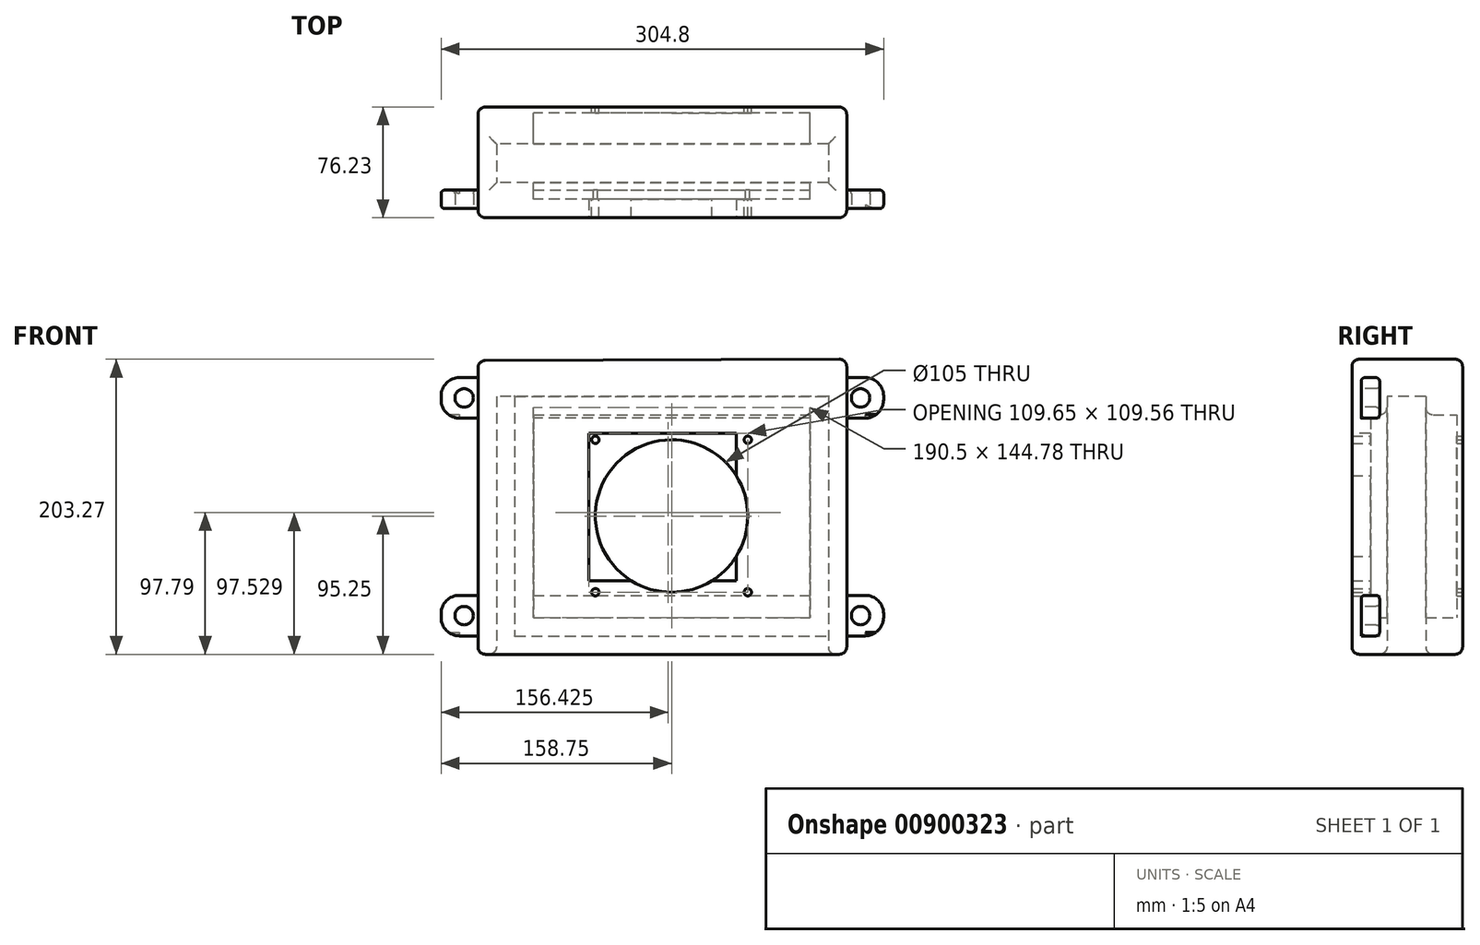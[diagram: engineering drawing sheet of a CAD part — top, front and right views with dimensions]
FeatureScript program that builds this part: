
annotation { "Feature Type Name" : "Feature", "Feature Type Description" : "" }
export const myFeature = defineFeature(function(context is Context, id is Id, definition is map)
    precondition{}
    {
        {
            var Q0;
            Q0=qCreatedBy(makeId("Front.planeOp"),FACE);
            var sketch = newSketch(context, id + "F0", { "sketchPlane" : qUnion([Q0])});
            skLineSegment(sketch, "E0", {"start": v(0, 202.37) * mm, "end": v(0, 0) * mm});
            skLineSegment(sketch, "E1", {"start": v(0, 0) * mm, "end": v(254, 0) * mm});
            skLineSegment(sketch, "E2", {"start": v(254, 0) * mm, "end": v(254, 203.3) * mm});
            skLineSegment(sketch, "E3", {"start": v(254, 203.3) * mm, "end": v(0, 202.37) * mm});
            skLineSegment(sketch, "E4.bottom", {"start": v(228.6, 165.1) * mm, "end": v(38.1, 165.1) * mm});
            skLineSegment(sketch, "E4.top", {"start": v(228.6, 25.4) * mm, "end": v(38.1, 25.4) * mm});
            skLineSegment(sketch, "E4.left", {"start": v(228.6, 165.1) * mm, "end": v(228.6, 25.4) * mm});
            skLineSegment(sketch, "E4.right", {"start": v(38.1, 165.1) * mm, "end": v(38.1, 25.4) * mm});
            skLineSegment(sketch, "E5.bottom", {"start": v(25.4, 177.8) * mm, "end": v(241.3, 177.8) * mm});
            skLineSegment(sketch, "E5.top", {"start": v(25.4, 12.7) * mm, "end": v(241.3, 12.7) * mm});
            skLineSegment(sketch, "E5.left", {"start": v(25.4, 177.8) * mm, "end": v(25.4, 12.7) * mm});
            skLineSegment(sketch, "E5.right", {"start": v(241.3, 177.8) * mm, "end": v(241.3, 12.7) * mm});
            skSolve(sketch);
        }
        {
            var Q0;
            Q0=makeQuery(id+"F0.imprint","IMPRINT",FACE,{"disambiguationData":[TD([[makeQuery(id+"F0.imprint","IMPRINT",EDGE,{"derivedFrom":sQuery(id+"F0.wireOp",EDGE,"E0")}),1.0]])]});
            var Q1;
            Q1=makeQuery(id+"F0.imprint","IMPRINT",FACE,{"disambiguationData":[TD([[makeQuery(id+"F0.imprint","IMPRINT",EDGE,{"derivedFrom":sQuery(id+"F0.wireOp",EDGE,"E4.bottom")}),-1.0]])]});
            extrude(context, id + "F1", {"entities" : qUnion([Q0, Q1]), "depth" : 76.2 * mm, "offsetDistance" : 25.4 * mm});
        }
        {
            var Q0;
            Q0=makeQuery(id+"F1.opExtrude","SWEPT_FACE",FACE,{"disambiguationData":[OSD([sQuery(id+"F0.wireOp",EDGE,"E1")])]});
            var sketch = newSketch(context, id + "F2", { "sketchPlane" : qUnion([Q0])});
            skLineSegment(sketch, "E6.bottom", {"start": v(12.7, 52.07) * mm, "end": v(241.3, 52.07) * mm});
            skLineSegment(sketch, "E6.top", {"start": v(12.7, 25.4) * mm, "end": v(241.3, 25.4) * mm});
            skLineSegment(sketch, "E6.left", {"start": v(12.7, 52.07) * mm, "end": v(12.7, 25.4) * mm});
            skLineSegment(sketch, "E6.right", {"start": v(241.3, 52.07) * mm, "end": v(241.3, 25.4) * mm});
            skSolve(sketch);
        }
        {
            var Q0;
            Q0=makeQuery(id+"F0.imprint","IMPRINT",FACE,{"disambiguationData":[TD([[makeQuery(id+"F0.imprint","IMPRINT",EDGE,{"derivedFrom":sQuery(id+"F0.wireOp",EDGE,"E4.bottom")}),-1.0]])]});
            var Q1;
            Q1=makeQuery(id+"F0.imprint","IMPRINT",FACE,{"disambiguationData":[TD([[makeQuery(id+"F0.imprint","IMPRINT",EDGE,{"derivedFrom":sQuery(id+"F0.wireOp",EDGE,"E4.bottom")}),1.0]])]});
            extrude(context, id + "F3", {"entities" : qUnion([Q0, Q1]), "operationType" : NewBodyOperationType.ADD, "oppositeDirection" : true, "depth" : 0.03 * mm, "offsetDistance" : 25.4 * mm, "hasSecondDirection" : true, "secondDirectionOppositeDirection" : false, "secondDirectionDepth" : 4 * mm});
        }
        {
            var Q0;
            Q0=makeQuery(id+"F3.opExtrude","CAP_FACE",FACE,{"disambiguationData":[OSD([sQuery(id+"F0.wireOp",EDGE,"E5.bottom"),sQuery(id+"F0.wireOp",EDGE,"E5.top"),sQuery(id+"F0.wireOp",EDGE,"E5.left"),sQuery(id+"F0.wireOp",EDGE,"E5.right")])],"isStart":false});
            var sketch = newSketch(context, id + "F4", { "sketchPlane" : qUnion([Q0])});
            skCircle(sketch, "E7", {"center": v(-133.35, 95.25) * mm, "radius": 52.5 * mm});
            skLineSegment(sketch, "E8", {"start": v(-133.35, 95.25) * mm, "end": v(-25.4, 95.25) * mm, "construction": true});
            skLineSegment(sketch, "E9", {"start": v(-133.35, 95.25) * mm, "end": v(-241.3, 95.25) * mm, "construction": true});
            skLineSegment(sketch, "E10", {"start": v(-133.35, 95.25) * mm, "end": v(-133.35, 12.7) * mm, "construction": true});
            skCircle(sketch, "E11", {"center": v(-185.85, 42.75) * mm, "radius": 2.54 * mm});
            skCircle(sketch, "E12", {"center": v(-185.85, 147.75) * mm, "radius": 2.54 * mm});
            skCircle(sketch, "E13", {"center": v(-80.85, 42.75) * mm, "radius": 2.54 * mm});
            skCircle(sketch, "E14", {"center": v(-80.85, 147.75) * mm, "radius": 2.54 * mm});
            skLineSegment(sketch, "E15", {"start": v(-185.85, 42.75) * mm, "end": v(-185.85, 95.25) * mm, "construction": true});
            skLineSegment(sketch, "E16", {"start": v(-185.85, 95.25) * mm, "end": v(-185.85, 147.75) * mm, "construction": true});
            skLineSegment(sketch, "E17", {"start": v(-185.85, 147.75) * mm, "end": v(-133.35, 147.75) * mm, "construction": true});
            skLineSegment(sketch, "E18", {"start": v(-133.35, 147.75) * mm, "end": v(-80.85, 147.75) * mm, "construction": true});
            skLineSegment(sketch, "E19", {"start": v(-80.85, 147.75) * mm, "end": v(-80.85, 177.8) * mm, "construction": true});
            skLineSegment(sketch, "E20", {"start": v(-80.85, 42.75) * mm, "end": v(-80.85, 12.7) * mm, "construction": true});
            skSolve(sketch);
        }
        {
            var Q0;
            Q0=makeQuery(id+"F4.imprint","IMPRINT",FACE,{"disambiguationData":[TD([[makeQuery(id+"F4.imprint","IMPRINT",EDGE,{"derivedFrom":sQuery(id+"F4.wireOp",EDGE,"E7")}),1.0]])]});
            var Q1;
            Q1=makeQuery(id+"F4.imprint","IMPRINT",FACE,{"disambiguationData":[TD([[makeQuery(id+"F4.imprint","IMPRINT",EDGE,{"derivedFrom":sQuery(id+"F4.wireOp",EDGE,"E11")}),1.0]])]});
            var Q2;
            Q2=makeQuery(id+"F4.imprint","IMPRINT",FACE,{"disambiguationData":[TD([[makeQuery(id+"F4.imprint","IMPRINT",EDGE,{"derivedFrom":sQuery(id+"F4.wireOp",EDGE,"E12")}),1.0]])]});
            var Q3;
            Q3=makeQuery(id+"F4.imprint","IMPRINT",FACE,{"disambiguationData":[TD([[makeQuery(id+"F4.imprint","IMPRINT",EDGE,{"derivedFrom":sQuery(id+"F4.wireOp",EDGE,"E13")}),1.0]])]});
            var Q4;
            Q4=makeQuery(id+"F4.imprint","IMPRINT",FACE,{"disambiguationData":[TD([[makeQuery(id+"F4.imprint","IMPRINT",EDGE,{"derivedFrom":sQuery(id+"F4.wireOp",EDGE,"E14")}),1.0]])]});
            extrude(context, id + "F5", {"entities" : qUnion([Q0, Q1, Q2, Q3, Q4]), "operationType" : NewBodyOperationType.REMOVE, "endBound" : BoundingType.THROUGH_ALL, "oppositeDirection" : true, "depth" : 25.4 * mm, "offsetDistance" : 25.4 * mm});
        }
        {
            var Q0;
            Q0=makeQuery(id+"F1.opExtrude","SWEPT_FACE",FACE,{"disambiguationData":[OSD([sQuery(id+"F0.wireOp",EDGE,"E0")])]});
            var sketch = newSketch(context, id + "F6", { "sketchPlane" : qUnion([Q0])});
            skLineSegment(sketch, "E21.bottom", {"start": v(69.85, 12.7) * mm, "end": v(57.15, 12.7) * mm});
            skLineSegment(sketch, "E21.top", {"start": v(69.85, 40.64) * mm, "end": v(57.15, 40.64) * mm});
            skLineSegment(sketch, "E21.left", {"start": v(69.85, 12.7) * mm, "end": v(69.85, 40.64) * mm});
            skLineSegment(sketch, "E21.right", {"start": v(57.15, 12.7) * mm, "end": v(57.15, 40.64) * mm});
            skLineSegment(sketch, "E22.bottom", {"start": v(69.85, 162.65) * mm, "end": v(57.15, 162.65) * mm});
            skLineSegment(sketch, "E22.top", {"start": v(69.85, 190.6) * mm, "end": v(57.15, 190.6) * mm});
            skLineSegment(sketch, "E22.left", {"start": v(69.85, 162.65) * mm, "end": v(69.85, 190.6) * mm});
            skLineSegment(sketch, "E22.right", {"start": v(57.15, 162.65) * mm, "end": v(57.15, 190.6) * mm});
            skSolve(sketch);
        }
        {
            var Q0;
            Q0=makeQuery(id+"F6.imprint","IMPRINT",FACE,{"disambiguationData":[TD([[makeQuery(id+"F6.imprint","IMPRINT",EDGE,{"derivedFrom":sQuery(id+"F6.wireOp",EDGE,"E21.bottom")}),-1.0]])]});
            var Q1;
            Q1=makeQuery(id+"F6.imprint","IMPRINT",FACE,{"disambiguationData":[TD([[makeQuery(id+"F6.imprint","IMPRINT",EDGE,{"derivedFrom":sQuery(id+"F6.wireOp",EDGE,"E22.bottom")}),-1.0]])]});
            var Q2;
            Q2=makeQuery(id+"F1.opExtrude","SWEPT_FACE",FACE,{"disambiguationData":[OSD([sQuery(id+"F0.wireOp",EDGE,"E2")])]});
            var Q3;
            Q3=makeQuery(id+"F1.opExtrude","SWEPT_FACE",FACE,{"disambiguationData":[OSD([sQuery(id+"F0.wireOp",EDGE,"E2")])]});
            extrude(context, id + "F7", {"entities" : qUnion([Q0, Q1]), "operationType" : NewBodyOperationType.ADD, "depth" : 25.4 * mm, "endBoundEntityFace" : qUnion([Q2]), "hasOffset" : true, "offsetDistance" : 25.4 * mm, "hasSecondDirection" : true, "secondDirectionBound" : SecondDirectionBoundingType.UP_TO_SURFACE, "secondDirectionOppositeDirection" : true, "secondDirectionDepth" : 25.4 * mm, "secondDirectionBoundEntityFace" : qUnion([Q3]), "hasSecondDirectionOffset" : true, "secondDirectionOffsetDistance" : 25.4 * mm, "secondDirectionOffsetOppositeDirection" : true});
        }
        {
            var Q0;
            {var subQ2=sQuery(id+"F6.wireOp",EDGE,"E21.left");Q0=makeQuery(id+"F7.boolean.opBoolean","SPLIT",FACE,{"disambiguationData":[TD([makeQuery(id+"F1.opExtrude","SWEPT_FACE",FACE,{"disambiguationData":[OSD([sQuery(id+"F0.wireOp",EDGE,"E2")])]})])],"derivedFrom":makeQuery(id+"F7.opExtrude","SWEPT_FACE",FACE,{"disambiguationData":[OSD([subQ2])]})});}
            var sketch = newSketch(context, id + "F8", { "sketchPlane" : qUnion([Q0])});
            skPoint(sketch, "E23.centerSnap0", {"position": v(279.4, 26.67) * mm});
            skCircle(sketch, "E24", {"center": v(-9.52, 26.67) * mm, "radius": 6.35 * mm});
            skCircle(sketch, "E25", {"center": v(263.53, 176.62) * mm, "radius": 6.35 * mm});
            skCircle(sketch, "E26", {"center": v(-9.52, 176.62) * mm, "radius": 6.35 * mm});
            skLineSegment(sketch, "E27", {"start": v(263.53, 176.62) * mm, "end": v(279.4, 176.62) * mm, "construction": true});
            skLineSegment(sketch, "E28", {"start": v(-9.52, 176.62) * mm, "end": v(-25.4, 176.62) * mm, "construction": true});
            skCircle(sketch, "E29", {"center": v(263.53, 26.67) * mm, "radius": 6.35 * mm});
            skSolve(sketch);
        }
        {
            var Q0;
            Q0=makeQuery(id+"F2.imprint","IMPRINT",FACE,{"disambiguationData":[TD([[makeQuery(id+"F2.imprint","IMPRINT",EDGE,{"derivedFrom":sQuery(id+"F2.wireOp",EDGE,"E6.bottom")}),-1.0]])]});
            var Q1;
            Q1=makeQuery(id+"F1.opExtrude","SWEPT_FACE",FACE,{"disambiguationData":[OSD([sQuery(id+"F0.wireOp",EDGE,"E4.bottom")])]});
            extrude(context, id + "F9", {"entities" : qUnion([Q0]), "operationType" : NewBodyOperationType.REMOVE, "endBound" : BoundingType.UP_TO_SURFACE, "oppositeDirection" : true, "depth" : 209.55 * mm, "endBoundEntityFace" : qUnion([Q1]), "hasOffset" : true, "offsetDistance" : 12.7 * mm, "offsetOppositeDirection" : true});
        }
        {
            var Q0;
            Q0=makeQuery(id+"F2.imprint","IMPRINT",FACE,{"disambiguationData":[TD([[makeQuery(id+"F2.imprint","IMPRINT",EDGE,{"derivedFrom":sQuery(id+"F2.wireOp",EDGE,"E6.bottom")}),1.0]])]});
            var sketch = newSketch(context, id + "F10", { "sketchPlane" : qUnion([Q0])});
            skCircle(sketch, "E30", {"center": v(127, 38.74) * mm, "radius": 22.1 * mm});
            skSolve(sketch);
        }
        {
            var Q0;
            {var subQ0=sQuery(id+"F10.wireOp",EDGE,"E30");var subQ1=makeQuery(id+"F2.imprint","IMPRINT",EDGE,{"derivedFrom":sQuery(id+"F2.wireOp",EDGE,"E6.bottom")});var subQ2=makeQuery(id+"F10.imprint","INTERSECT",VERTEX,{"disambiguationData":[OD(0.0)],"derivedFrom":[subQ1,subQ0]});Q0=makeQuery(id+"F10.imprint","IMPRINT",FACE,{"disambiguationData":[TD([[makeQuery(id+"F10.imprint","IMPRINT",EDGE,{"disambiguationData":[TD([[subQ2,1.0]])],"derivedFrom":subQ0}),1.0]])]});}
            var Q1;
            {var subQ0=sQuery(id+"F10.wireOp",EDGE,"E30");var subQ1=makeQuery(id+"F2.imprint","IMPRINT",EDGE,{"derivedFrom":sQuery(id+"F2.wireOp",EDGE,"E6.top")});var subQ2=makeQuery(id+"F10.imprint","INTERSECT",VERTEX,{"disambiguationData":[OD(0.0)],"derivedFrom":[subQ1,subQ0]});Q1=makeQuery(id+"F10.imprint","IMPRINT",FACE,{"disambiguationData":[TD([[makeQuery(id+"F10.imprint","IMPRINT",EDGE,{"disambiguationData":[TD([[subQ2,-1.0]])],"derivedFrom":subQ0}),1.0]])]});}
            var Q2;
            Q2=sQuery(id+"F10.wireOp",EDGE,"E30");
            extrude(context, id + "F11", {"entities" : qUnion([Q0, Q1]), "operationType" : NewBodyOperationType.REMOVE, "surfaceEntities" : qUnion([Q2]), "oppositeDirection" : true, "depth" : 12.7 * mm, "offsetDistance" : 25.4 * mm});
        }
        {
            var Q0;
            Q0=makeQuery(id+"F1.opExtrude","CAP_FACE",FACE,{"disambiguationData":[OSD([sQuery(id+"F0.wireOp",EDGE,"E0"),sQuery(id+"F0.wireOp",EDGE,"E1"),sQuery(id+"F0.wireOp",EDGE,"E2"),sQuery(id+"F0.wireOp",EDGE,"E3"),sQuery(id+"F0.wireOp",EDGE,"E4.bottom"),sQuery(id+"F0.wireOp",EDGE,"E4.top"),sQuery(id+"F0.wireOp",EDGE,"E4.left"),sQuery(id+"F0.wireOp",EDGE,"E4.right")])],"isStart":false});
            var sketch = newSketch(context, id + "F12", { "sketchPlane" : qUnion([Q0])});
            skLineSegment(sketch, "E31.bottom", {"start": v(177.8, 152.3) * mm, "end": v(76.2, 152.3) * mm});
            skLineSegment(sketch, "E31.top", {"start": v(177.8, 50.7) * mm, "end": v(76.2, 50.7) * mm});
            skLineSegment(sketch, "E31.left", {"start": v(177.8, 152.3) * mm, "end": v(177.8, 50.7) * mm});
            skLineSegment(sketch, "E31.right", {"start": v(76.2, 152.3) * mm, "end": v(76.2, 50.7) * mm});
            skLineSegment(sketch, "E32", {"start": v(177.8, 152.3) * mm, "end": v(177.8, 203.02) * mm, "construction": true});
            skLineSegment(sketch, "E33", {"start": v(177.8, 50.7) * mm, "end": v(177.8, 0) * mm, "construction": true});
            skLineSegment(sketch, "E34", {"start": v(177.8, 152.3) * mm, "end": v(254, 152.3) * mm, "construction": true});
            skLineSegment(sketch, "E35", {"start": v(76.2, 152.3) * mm, "end": v(0, 152.3) * mm, "construction": true});
            skSolve(sketch);
        }
        {
            var Q0;
            Q0=makeQuery(id+"F12.imprint","IMPRINT",FACE,{"disambiguationData":[TD([[makeQuery(id+"F12.imprint","IMPRINT",EDGE,{"derivedFrom":sQuery(id+"F12.wireOp",EDGE,"E31.bottom")}),-1.0]])]});
            extrude(context, id + "F13", {"entities" : qUnion([Q0]), "operationType" : NewBodyOperationType.ADD, "oppositeDirection" : true, "depth" : 12.7 * mm, "offsetDistance" : 25.4 * mm});
        }
        {
            var Q0;
            Q0=makeQuery(id+"F1.opExtrude","CAP_FACE",FACE,{"disambiguationData":[OSD([sQuery(id+"F0.wireOp",EDGE,"E0"),sQuery(id+"F0.wireOp",EDGE,"E1"),sQuery(id+"F0.wireOp",EDGE,"E2"),sQuery(id+"F0.wireOp",EDGE,"E3"),sQuery(id+"F0.wireOp",EDGE,"E4.bottom"),sQuery(id+"F0.wireOp",EDGE,"E4.top"),sQuery(id+"F0.wireOp",EDGE,"E4.left"),sQuery(id+"F0.wireOp",EDGE,"E4.right")])],"isStart":true});
            var Q1;
            Q1=makeQuery(id+"F1.opExtrude","SWEPT_FACE",FACE,{"disambiguationData":[OSD([sQuery(id+"F0.wireOp",EDGE,"E1")])]});
            var Q2;
            Q2=makeQuery(id+"F1.opExtrude","SWEPT_FACE",FACE,{"disambiguationData":[OSD([sQuery(id+"F0.wireOp",EDGE,"E3")])]});
            var Q3;
            Q3=makeQuery(id+"F9.boolean.opBoolean","INTERSECT",EDGE,{"derivedFrom":[makeQuery(id+"F1.opExtrude","SWEPT_FACE",FACE,{"disambiguationData":[OSD([sQuery(id+"F0.wireOp",EDGE,"E4.bottom")])]}),makeQuery(id+"F9.opExtrude","SWEPT_FACE",FACE,{"disambiguationData":[OSD([sQuery(id+"F2.wireOp",EDGE,"E6.top")])]})]});
            var Q4;
            Q4=makeQuery(id+"F9.boolean.opBoolean","INTERSECT",EDGE,{"derivedFrom":[makeQuery(id+"F1.opExtrude","SWEPT_FACE",FACE,{"disambiguationData":[OSD([sQuery(id+"F0.wireOp",EDGE,"E4.bottom")])]}),makeQuery(id+"F9.opExtrude","SWEPT_FACE",FACE,{"disambiguationData":[OSD([sQuery(id+"F2.wireOp",EDGE,"E6.bottom")])]})]});
            var Q5;
            Q5=makeQuery(id+"F1.opExtrude","CAP_EDGE",EDGE,{"disambiguationData":[OSD([sQuery(id+"F0.wireOp",EDGE,"E0")])],"isStart":false});
            var Q6;
            Q6=makeQuery(id+"F1.opExtrude","CAP_EDGE",EDGE,{"disambiguationData":[OSD([sQuery(id+"F0.wireOp",EDGE,"E2")])],"isStart":false});
            fillet(context, id + "F14", {"entities" : qUnion([Q0, Q1, Q2, Q3, Q4, Q5, Q6]), "radius" : 5.08 * mm, "tangentPropagation" : true, "allowEdgeOverflow" : false});
        }
        {
            var Q0;
            Q0=makeQuery(id+"F8.imprint","IMPRINT",FACE,{"disambiguationData":[TD([[makeQuery(id+"F8.imprint","IMPRINT",EDGE,{"derivedFrom":sQuery(id+"F8.wireOp",EDGE,"E24")}),1.0]])]});
            var Q1;
            Q1=makeQuery(id+"F8.imprint","IMPRINT",FACE,{"disambiguationData":[TD([[makeQuery(id+"F8.imprint","IMPRINT",EDGE,{"derivedFrom":sQuery(id+"F8.wireOp",EDGE,"E26")}),1.0]])]});
            var Q2;
            Q2=makeQuery(id+"F8.imprint","IMPRINT",FACE,{"disambiguationData":[TD([[makeQuery(id+"F8.imprint","IMPRINT",EDGE,{"derivedFrom":sQuery(id+"F8.wireOp",EDGE,"E25")}),1.0]])]});
            var Q3;
            Q3=makeQuery(id+"F8.imprint","IMPRINT",FACE,{"disambiguationData":[TD([[makeQuery(id+"F8.imprint","IMPRINT",EDGE,{"derivedFrom":sQuery(id+"F8.wireOp",EDGE,"E29")}),1.0]])]});
            var Q4;
            Q4=sQuery(id+"F8.wireOp",EDGE,"E24");
            extrude(context, id + "F15", {"entities" : qUnion([Q0, Q1, Q2, Q3]), "operationType" : NewBodyOperationType.REMOVE, "surfaceEntities" : qUnion([Q4]), "endBound" : BoundingType.THROUGH_ALL, "oppositeDirection" : true, "depth" : 25.4 * mm, "offsetDistance" : 25.4 * mm});
        }
        {
            var Q0;
            Q0=makeQuery(id+"F7.opExtrude","CAP_EDGE",EDGE,{"disambiguationData":[OSD([sQuery(id+"F6.wireOp",EDGE,"E22.top")])],"isStart":true});
            var Q1;
            Q1=makeQuery(id+"F7.opExtrude","CAP_EDGE",EDGE,{"disambiguationData":[OSD([sQuery(id+"F6.wireOp",EDGE,"E22.bottom")])],"isStart":true});
            var Q2;
            Q2=makeQuery(id+"F7.opExtrude","CAP_EDGE",EDGE,{"disambiguationData":[OSD([sQuery(id+"F6.wireOp",EDGE,"E21.top")])],"isStart":true});
            var Q3;
            Q3=makeQuery(id+"F7.opExtrude","CAP_EDGE",EDGE,{"disambiguationData":[OSD([sQuery(id+"F6.wireOp",EDGE,"E21.bottom")])],"isStart":true});
            var Q4;
            Q4=makeQuery(id+"F7.opExtrude","CAP_EDGE",EDGE,{"disambiguationData":[OSD([sQuery(id+"F6.wireOp",EDGE,"E21.top")])],"isStart":false});
            var Q5;
            Q5=makeQuery(id+"F7.opExtrude","CAP_EDGE",EDGE,{"disambiguationData":[OSD([sQuery(id+"F6.wireOp",EDGE,"E21.bottom")])],"isStart":false});
            var Q6;
            Q6=makeQuery(id+"F7.opExtrude","CAP_EDGE",EDGE,{"disambiguationData":[OSD([sQuery(id+"F6.wireOp",EDGE,"E22.bottom")])],"isStart":false});
            var Q7;
            Q7=makeQuery(id+"F7.opExtrude","CAP_EDGE",EDGE,{"disambiguationData":[OSD([sQuery(id+"F6.wireOp",EDGE,"E22.top")])],"isStart":false});
            fillet(context, id + "F16", {"entities" : qUnion([Q0, Q1, Q2, Q3, Q4, Q5, Q6, Q7]), "radius" : 12.7 * mm, "tangentPropagation" : true, "allowEdgeOverflow" : false});
        }
        {
            var Q0;
            Q0=makeQuery(id+"F15.boolean.opBoolean","COPY",EDGE,{"derivedFrom":makeQuery(id+"F15.opExtrude","CAP_EDGE",EDGE,{"disambiguationData":[OSD([sQuery(id+"F8.wireOp",EDGE,"E26")])],"isStart":true})});
            var Q1;
            {var subQ2=sQuery(id+"F6.wireOp",EDGE,"E22.right");Q1=makeQuery(id+"F15.boolean.opBoolean","INTERSECT",EDGE,{"derivedFrom":[makeQuery(id+"F7.boolean.opBoolean","SPLIT",FACE,{"disambiguationData":[TD([makeQuery(id+"F1.opExtrude","SWEPT_FACE",FACE,{"disambiguationData":[OSD([sQuery(id+"F0.wireOp",EDGE,"E0")])]})])],"derivedFrom":makeQuery(id+"F7.opExtrude","SWEPT_FACE",FACE,{"disambiguationData":[OSD([subQ2])]})}),makeQuery(id+"F15.opExtrude","SWEPT_FACE",FACE,{"disambiguationData":[OSD([sQuery(id+"F8.wireOp",EDGE,"E26")])]})]});}
            var Q2;
            {var subQ1=sQuery(id+"F6.wireOp",EDGE,"E21.right");Q2=makeQuery(id+"F15.boolean.opBoolean","INTERSECT",EDGE,{"derivedFrom":[makeQuery(id+"F7.boolean.opBoolean","SPLIT",FACE,{"disambiguationData":[TD([makeQuery(id+"F1.opExtrude","SWEPT_FACE",FACE,{"disambiguationData":[OSD([sQuery(id+"F0.wireOp",EDGE,"E0")])]})])],"derivedFrom":makeQuery(id+"F7.opExtrude","SWEPT_FACE",FACE,{"disambiguationData":[OSD([subQ1])]})}),makeQuery(id+"F15.opExtrude","SWEPT_FACE",FACE,{"disambiguationData":[OSD([sQuery(id+"F8.wireOp",EDGE,"E24")])]})]});}
            var Q3;
            Q3=makeQuery(id+"F15.boolean.opBoolean","COPY",EDGE,{"derivedFrom":makeQuery(id+"F15.opExtrude","CAP_EDGE",EDGE,{"disambiguationData":[OSD([sQuery(id+"F8.wireOp",EDGE,"E24")])],"isStart":true})});
            var Q4;
            Q4=makeQuery(id+"F15.boolean.opBoolean","COPY",EDGE,{"derivedFrom":makeQuery(id+"F15.opExtrude","CAP_EDGE",EDGE,{"disambiguationData":[OSD([sQuery(id+"F8.wireOp",EDGE,"E25")])],"isStart":true})});
            var Q5;
            Q5=makeQuery(id+"F15.boolean.opBoolean","COPY",EDGE,{"derivedFrom":makeQuery(id+"F15.opExtrude","CAP_EDGE",EDGE,{"disambiguationData":[OSD([sQuery(id+"F8.wireOp",EDGE,"E29")])],"isStart":true})});
            var Q6;
            {var subQ1=sQuery(id+"F6.wireOp",EDGE,"E22.right");Q6=makeQuery(id+"F15.boolean.opBoolean","INTERSECT",EDGE,{"derivedFrom":[makeQuery(id+"F7.boolean.opBoolean","SPLIT",FACE,{"disambiguationData":[TD([makeQuery(id+"F1.opExtrude","SWEPT_FACE",FACE,{"disambiguationData":[OSD([sQuery(id+"F0.wireOp",EDGE,"E2")])]})])],"derivedFrom":makeQuery(id+"F7.opExtrude","SWEPT_FACE",FACE,{"disambiguationData":[OSD([subQ1])]})}),makeQuery(id+"F15.opExtrude","SWEPT_FACE",FACE,{"disambiguationData":[OSD([sQuery(id+"F8.wireOp",EDGE,"E25")])]})]});}
            var Q7;
            {var subQ2=sQuery(id+"F6.wireOp",EDGE,"E21.right");Q7=makeQuery(id+"F15.boolean.opBoolean","INTERSECT",EDGE,{"derivedFrom":[makeQuery(id+"F7.boolean.opBoolean","SPLIT",FACE,{"disambiguationData":[TD([makeQuery(id+"F1.opExtrude","SWEPT_FACE",FACE,{"disambiguationData":[OSD([sQuery(id+"F0.wireOp",EDGE,"E2")])]})])],"derivedFrom":makeQuery(id+"F7.opExtrude","SWEPT_FACE",FACE,{"disambiguationData":[OSD([subQ2])]})}),makeQuery(id+"F15.opExtrude","SWEPT_FACE",FACE,{"disambiguationData":[OSD([sQuery(id+"F8.wireOp",EDGE,"E29")])]})]});}
            var Q8;
            {var subQ1=sQuery(id+"F6.wireOp",EDGE,"E22.left");var subQ2=sQuery(id+"F6.wireOp",EDGE,"E22.top");Q8=makeQuery(id+"F16.opFillet","BLEND_EDGE",EDGE,{"blendedFrom":[makeQuery(id+"F7.opExtrude","CAP_EDGE",EDGE,{"disambiguationData":[OSD([subQ2])],"isStart":true}),makeQuery(id+"F7.boolean.opBoolean","SPLIT",FACE,{"disambiguationData":[TD([makeQuery(id+"F1.opExtrude","SWEPT_FACE",FACE,{"disambiguationData":[OSD([sQuery(id+"F0.wireOp",EDGE,"E2")])]})])],"derivedFrom":makeQuery(id+"F7.opExtrude","SWEPT_FACE",FACE,{"disambiguationData":[OSD([subQ1])]})})],"blendedInto":[makeQuery(id+"F7.boolean.opBoolean","SPLIT",FACE,{"disambiguationData":[TD([makeQuery(id+"F1.opExtrude","SWEPT_FACE",FACE,{"disambiguationData":[OSD([sQuery(id+"F0.wireOp",EDGE,"E2")])]})])],"derivedFrom":makeQuery(id+"F7.opExtrude","SWEPT_FACE",FACE,{"disambiguationData":[OSD([subQ1])]})})]});}
            var Q9;
            {var subQ0=sQuery(id+"F6.wireOp",EDGE,"E21.top");var subQ2=sQuery(id+"F6.wireOp",EDGE,"E21.left");Q9=makeQuery(id+"F16.opFillet","BLEND_EDGE",EDGE,{"blendedFrom":[makeQuery(id+"F7.opExtrude","CAP_EDGE",EDGE,{"disambiguationData":[OSD([subQ0])],"isStart":true}),makeQuery(id+"F7.boolean.opBoolean","SPLIT",FACE,{"disambiguationData":[TD([makeQuery(id+"F1.opExtrude","SWEPT_FACE",FACE,{"disambiguationData":[OSD([sQuery(id+"F0.wireOp",EDGE,"E2")])]})])],"derivedFrom":makeQuery(id+"F7.opExtrude","SWEPT_FACE",FACE,{"disambiguationData":[OSD([subQ2])]})})],"blendedInto":[makeQuery(id+"F7.boolean.opBoolean","SPLIT",FACE,{"disambiguationData":[TD([makeQuery(id+"F1.opExtrude","SWEPT_FACE",FACE,{"disambiguationData":[OSD([sQuery(id+"F0.wireOp",EDGE,"E2")])]})])],"derivedFrom":makeQuery(id+"F7.opExtrude","SWEPT_FACE",FACE,{"disambiguationData":[OSD([subQ2])]})})]});}
            var Q10;
            {var subQ0=sQuery(id+"F6.wireOp",EDGE,"E21.bottom");var subQ1=sQuery(id+"F6.wireOp",EDGE,"E21.left");Q10=makeQuery(id+"F16.opFillet","BLEND_EDGE",EDGE,{"blendedFrom":[makeQuery(id+"F7.opExtrude","CAP_EDGE",EDGE,{"disambiguationData":[OSD([subQ0])],"isStart":false}),makeQuery(id+"F7.boolean.opBoolean","SPLIT",FACE,{"disambiguationData":[TD([makeQuery(id+"F1.opExtrude","SWEPT_FACE",FACE,{"disambiguationData":[OSD([sQuery(id+"F0.wireOp",EDGE,"E0")])]})])],"derivedFrom":makeQuery(id+"F7.opExtrude","SWEPT_FACE",FACE,{"disambiguationData":[OSD([subQ1])]})})],"blendedInto":[makeQuery(id+"F7.boolean.opBoolean","SPLIT",FACE,{"disambiguationData":[TD([makeQuery(id+"F1.opExtrude","SWEPT_FACE",FACE,{"disambiguationData":[OSD([sQuery(id+"F0.wireOp",EDGE,"E0")])]})])],"derivedFrom":makeQuery(id+"F7.opExtrude","SWEPT_FACE",FACE,{"disambiguationData":[OSD([subQ1])]})})]});}
            var Q11;
            {var subQ1=sQuery(id+"F6.wireOp",EDGE,"E22.bottom");var subQ2=sQuery(id+"F6.wireOp",EDGE,"E22.left");Q11=makeQuery(id+"F16.opFillet","BLEND_EDGE",EDGE,{"blendedFrom":[makeQuery(id+"F7.opExtrude","CAP_EDGE",EDGE,{"disambiguationData":[OSD([subQ1])],"isStart":false}),makeQuery(id+"F7.boolean.opBoolean","SPLIT",FACE,{"disambiguationData":[TD([makeQuery(id+"F1.opExtrude","SWEPT_FACE",FACE,{"disambiguationData":[OSD([sQuery(id+"F0.wireOp",EDGE,"E0")])]})])],"derivedFrom":makeQuery(id+"F7.opExtrude","SWEPT_FACE",FACE,{"disambiguationData":[OSD([subQ2])]})})],"blendedInto":[makeQuery(id+"F7.boolean.opBoolean","SPLIT",FACE,{"disambiguationData":[TD([makeQuery(id+"F1.opExtrude","SWEPT_FACE",FACE,{"disambiguationData":[OSD([sQuery(id+"F0.wireOp",EDGE,"E0")])]})])],"derivedFrom":makeQuery(id+"F7.opExtrude","SWEPT_FACE",FACE,{"disambiguationData":[OSD([subQ2])]})})]});}
            var Q12;
            {var subQ0=sQuery(id+"F6.wireOp",EDGE,"E22.top");var subQ2=sQuery(id+"F6.wireOp",EDGE,"E22.right");Q12=makeQuery(id+"F16.opFillet","BLEND_EDGE",EDGE,{"blendedFrom":[makeQuery(id+"F7.opExtrude","CAP_EDGE",EDGE,{"disambiguationData":[OSD([subQ0])],"isStart":false}),makeQuery(id+"F7.boolean.opBoolean","SPLIT",FACE,{"disambiguationData":[TD([makeQuery(id+"F1.opExtrude","SWEPT_FACE",FACE,{"disambiguationData":[OSD([sQuery(id+"F0.wireOp",EDGE,"E0")])]})])],"derivedFrom":makeQuery(id+"F7.opExtrude","SWEPT_FACE",FACE,{"disambiguationData":[OSD([subQ2])]})})],"blendedInto":[makeQuery(id+"F7.boolean.opBoolean","SPLIT",FACE,{"disambiguationData":[TD([makeQuery(id+"F1.opExtrude","SWEPT_FACE",FACE,{"disambiguationData":[OSD([sQuery(id+"F0.wireOp",EDGE,"E0")])]})])],"derivedFrom":makeQuery(id+"F7.opExtrude","SWEPT_FACE",FACE,{"disambiguationData":[OSD([subQ2])]})})]});}
            var Q13;
            {var subQ1=sQuery(id+"F6.wireOp",EDGE,"E21.right");var subQ2=sQuery(id+"F6.wireOp",EDGE,"E21.top");Q13=makeQuery(id+"F16.opFillet","BLEND_EDGE",EDGE,{"blendedFrom":[makeQuery(id+"F7.opExtrude","CAP_EDGE",EDGE,{"disambiguationData":[OSD([subQ2])],"isStart":false}),makeQuery(id+"F7.boolean.opBoolean","SPLIT",FACE,{"disambiguationData":[TD([makeQuery(id+"F1.opExtrude","SWEPT_FACE",FACE,{"disambiguationData":[OSD([sQuery(id+"F0.wireOp",EDGE,"E0")])]})])],"derivedFrom":makeQuery(id+"F7.opExtrude","SWEPT_FACE",FACE,{"disambiguationData":[OSD([subQ1])]})})],"blendedInto":[makeQuery(id+"F7.boolean.opBoolean","SPLIT",FACE,{"disambiguationData":[TD([makeQuery(id+"F1.opExtrude","SWEPT_FACE",FACE,{"disambiguationData":[OSD([sQuery(id+"F0.wireOp",EDGE,"E0")])]})])],"derivedFrom":makeQuery(id+"F7.opExtrude","SWEPT_FACE",FACE,{"disambiguationData":[OSD([subQ1])]})})]});}
            var Q14;
            {var subQ0=sQuery(id+"F6.wireOp",EDGE,"E21.bottom");var subQ1=sQuery(id+"F6.wireOp",EDGE,"E21.right");Q14=makeQuery(id+"F7.boolean.opBoolean","SPLIT",EDGE,{"disambiguationData":[TD([makeQuery(id+"F1.opExtrude","SWEPT_FACE",FACE,{"disambiguationData":[OSD([sQuery(id+"F0.wireOp",EDGE,"E2")])]})])],"derivedFrom":makeQuery(id+"F7.opExtrude","SWEPT_EDGE",EDGE,{"disambiguationData":[OSD([subQ0,subQ1])]})});}
            var Q15;
            {var subQ0=sQuery(id+"F6.wireOp",EDGE,"E22.bottom");var subQ1=sQuery(id+"F6.wireOp",EDGE,"E22.right");Q15=makeQuery(id+"F7.boolean.opBoolean","SPLIT",EDGE,{"disambiguationData":[TD([makeQuery(id+"F1.opExtrude","SWEPT_FACE",FACE,{"disambiguationData":[OSD([sQuery(id+"F0.wireOp",EDGE,"E2")])]})])],"derivedFrom":makeQuery(id+"F7.opExtrude","SWEPT_EDGE",EDGE,{"disambiguationData":[OSD([subQ0,subQ1])]})});}
            fillet(context, id + "F17", {"entities" : qUnion([Q0, Q1, Q2, Q3, Q4, Q5, Q6, Q7, Q8, Q9, Q10, Q11, Q12, Q13, Q14, Q15]), "radius" : 2.54 * mm, "tangentPropagation" : true, "allowEdgeOverflow" : false});
        }
    });
